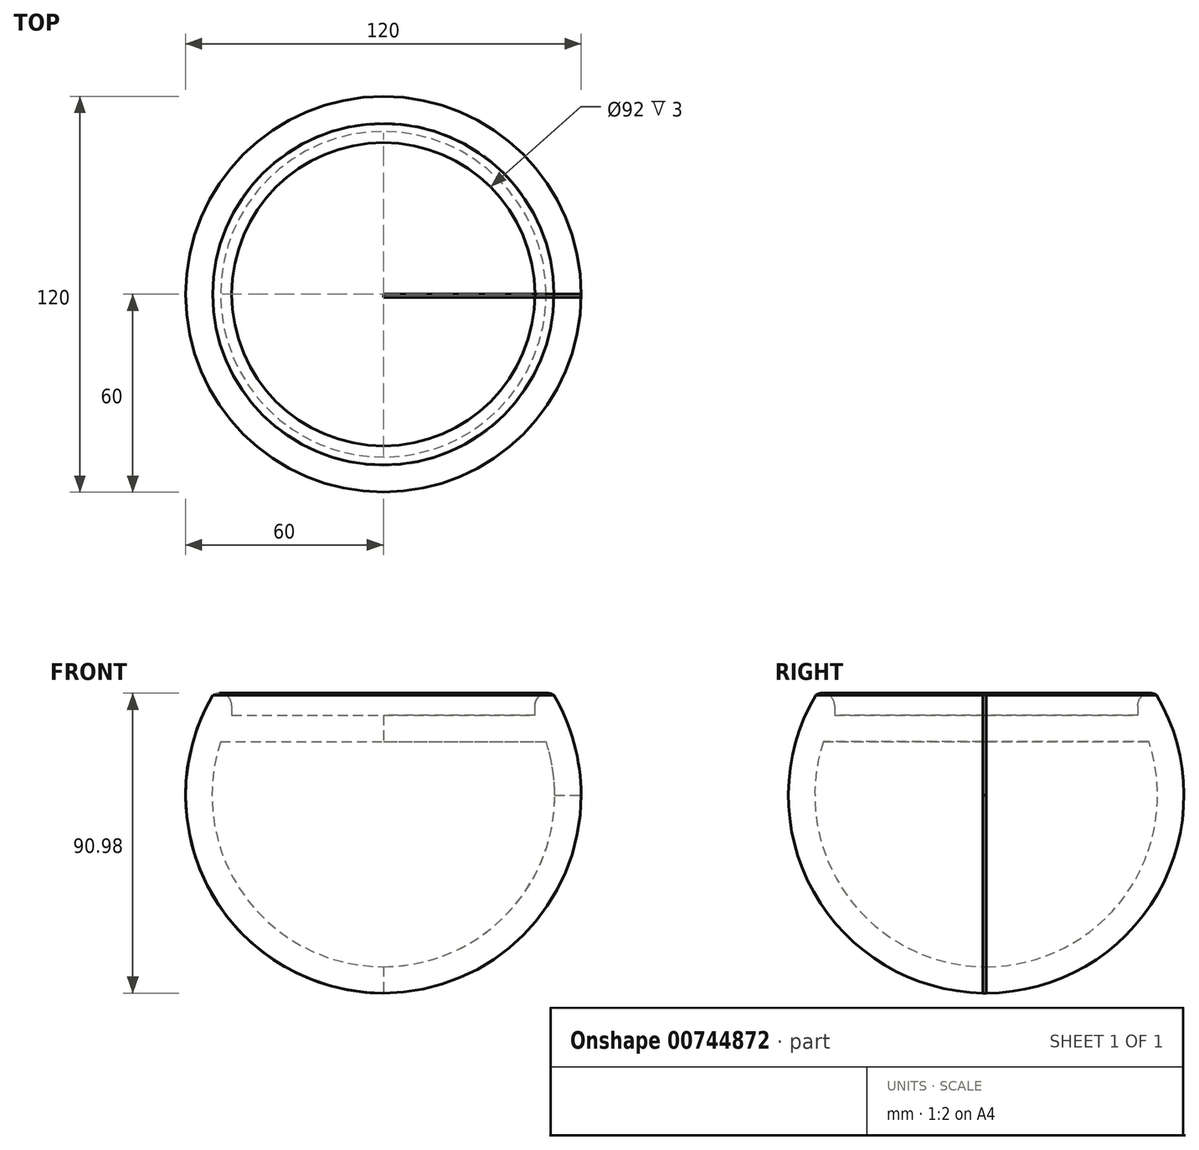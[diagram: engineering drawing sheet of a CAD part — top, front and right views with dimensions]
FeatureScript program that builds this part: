
annotation { "Feature Type Name" : "Feature", "Feature Type Description" : "" }
export const myFeature = defineFeature(function(context is Context, id is Id, definition is map)
    precondition{}
    {
        {
            var Q0;
            Q0=qCreatedBy(makeId("Front.planeOp"),FACE);
            var sketch = newSketch(context, id + "F0", { "sketchPlane" : qUnion([Q0])});
            skCircle(sketch, "E0", {"center": v(0, 0) * mm, "radius": 60 * mm});
            skCircle(sketch, "E1", {"center": v(0, 0) * mm, "radius": 52 * mm});
            skLineSegment(sketch, "E2", {"start": v(0, -52) * mm, "end": v(0, -60) * mm});
            skLineSegment(sketch, "E3", {"start": v(46, 24.25) * mm, "end": v(0, 24.25) * mm});
            skLineSegment(sketch, "E4", {"start": v(0, 24.25) * mm, "end": v(0, 16.25) * mm});
            skLineSegment(sketch, "E5", {"start": v(0, 16.25) * mm, "end": v(49.4, 16.25) * mm});
            skLineSegment(sketch, "E6", {"start": v(0, -52) * mm, "end": v(0, 52) * mm, "construction": true});
            skLineSegment(sketch, "E7", {"start": v(52, 0) * mm, "end": v(60, 0) * mm});
            skLineSegment(sketch, "E8", {"start": v(60, -38.84) * mm, "end": v(60, -2.15) * mm, "construction": true});
            skLineSegment(sketch, "E9", {"start": v(46, 22.44) * mm, "end": v(46, 24.25) * mm});
            skLineSegment(sketch, "E10", {"start": v(46, 24.25) * mm, "end": v(46, 27.25) * mm});
            skLineSegment(sketch, "E11", {"start": v(46, 27.25) * mm, "end": v(53.46, 27.25) * mm});
            skArc(sketch, "E12", {"start": v(53.46, 27.25) * mm, "mid": v(49.73, 30.98) * mm, "end": v(46, 27.25) * mm});
            skSolve(sketch);
        }
        {
            var Q0;
            Q0=qCreatedBy(makeId("Top.planeOp"),FACE);
            var sketch = newSketch(context, id + "F1", { "sketchPlane" : qUnion([Q0])});
            skCircle(sketch, "E13", {"center": v(0, 0) * mm, "radius": 26.97 * mm});
            skSolve(sketch);
        }
        {
            var Q0;
            {var subQ0=sQuery(id+"F0.wireOp",EDGE,"E3");Q0=makeQuery(id+"F0.imprint","IMPRINT",FACE,{"disambiguationData":[TD([[makeQuery(id+"F0.imprint","IMPRINT",EDGE,{"derivedFrom":subQ0}),1.0]])]});}
            var Q1;
            {var subQ0=sQuery(id+"F0.wireOp",EDGE,"E2");Q1=makeQuery(id+"F0.imprint","IMPRINT",FACE,{"disambiguationData":[TD([[makeQuery(id+"F0.imprint","IMPRINT",EDGE,{"derivedFrom":subQ0}),1.0]])]});}
            var Q2;
            {var subQ4=sQuery(id+"F0.wireOp",EDGE,"E7");Q2=makeQuery(id+"F0.imprint","IMPRINT",FACE,{"disambiguationData":[TD([[makeQuery(id+"F0.imprint","IMPRINT",EDGE,{"derivedFrom":subQ4}),1.0]])]});}
            var Q3;
            {var subQ1=sQuery(id+"F0.wireOp",EDGE,"VBpqcDpQ-XOw6-rAqD-s8CS-33bf4lKA4cVg");Q3=makeQuery(id+"F0.imprint","IMPRINT",FACE,{"disambiguationData":[TD([[makeQuery(id+"F0.imprint","IMPRINT",EDGE,{"derivedFrom":subQ1}),1.0]])]});}
            var Q4;
            {var subQ1=sQuery(id+"F0.wireOp",EDGE,"E11");Q4=makeQuery(id+"F0.imprint","IMPRINT",FACE,{"disambiguationData":[TD([[makeQuery(id+"F0.imprint","IMPRINT",EDGE,{"derivedFrom":subQ1}),1.0]])]});}
            var Q5;
            {var subQ3=sQuery(id+"F0.wireOp",EDGE,"zluPvVJ1-kkif-yVi0-dsCT-wnojSNXywTUM");Q5=makeQuery(id+"F0.imprint","IMPRINT",FACE,{"disambiguationData":[TD([[makeQuery(id+"F0.imprint","IMPRINT",EDGE,{"derivedFrom":subQ3}),-1.0]])]});}
            var Q6;
            Q6=sQuery(id+"F1.wireOp",EDGE,"E13");
            revolve(context, id + "F2", {"surfaceOperationType" : NewSurfaceOperationType.NEW, "entities" : qUnion([Q0, Q1, Q2, Q3, Q4, Q5]), "axis" : qUnion([Q6]), "revolveType" : RevolveType.FULL});
        }
        {
            var Q0;
            {var subQ0=sQuery(id+"F0.wireOp",EDGE,"E3");Q0=makeQuery(id+"F0.imprint","IMPRINT",FACE,{"disambiguationData":[TD([[makeQuery(id+"F0.imprint","IMPRINT",EDGE,{"derivedFrom":subQ0}),1.0]])]});}
            var Q1;
            {var subQ1=sQuery(id+"F0.wireOp",EDGE,"E11");Q1=makeQuery(id+"F0.imprint","IMPRINT",FACE,{"disambiguationData":[TD([[makeQuery(id+"F0.imprint","IMPRINT",EDGE,{"derivedFrom":subQ1}),1.0]])]});}
            var Q2;
            {var subQ0=sQuery(id+"F0.wireOp",EDGE,"E7");Q2=makeQuery(id+"F0.imprint","IMPRINT",FACE,{"disambiguationData":[TD([[makeQuery(id+"F0.imprint","IMPRINT",EDGE,{"derivedFrom":subQ0}),1.0]])]});}
            extrude(context, id + "F3", {"entities" : qUnion([Q0, Q1, Q2]), "depth" : 1 * mm, "offsetDistance" : 25 * mm});
        }
        {
            var Q0;
            {var subQ0=sQuery(id+"F0.wireOp",EDGE,"E2");Q0=makeQuery(id+"F0.imprint","IMPRINT",FACE,{"disambiguationData":[TD([[makeQuery(id+"F0.imprint","IMPRINT",EDGE,{"derivedFrom":subQ0}),1.0]])]});}
            extrude(context, id + "F4", {"entities" : qUnion([Q0]), "depth" : 1 * mm, "offsetDistance" : 25 * mm});
        }
    });
